# Revit family: SH-4502
name_source: partatom
category: Lighting Fixtures
revit_build: Autodesk Revit 2017 (Build: 20160225_1515(x64)
units: mm (PartAtom-declared; Revit-internal decimal feet)

## family parameters
Cut with Voids When Loaded = No
Host = Face
Light Source = Yes
Part Type = Normal
Room Calculation Point = No
Round Connector Dimension = Use Diameter
Shared = No

## types (2) — shared parameters
Body Material = Aluminum
Color Filter = 16777215
Default Elevation = 121.9 cm
Diffuser = Diffuser
Diffuser Material = Polycarbonate-anti uv
Dimming Lamp Color Temperature Shift = <None>
Emit Shape Visible in Rendering = No
Emit from Circle Diameter = 61.0 cm
Height = 33.6 cm
IP = IP44
Lamp = E27
Length = 22.7 cm
Manufacturer = SHOA
Model = SH-4502
Photometric Web File = 4376_V-TAC7WLEDBulbE27A60Thermoplastic3000K_1-5117.ies
Protection Class = Class I
Tilt Angle = 90.00°
URL = https://www.shoaco.com
Voltage/Frequency = 230v/50hz
Wattage. = 0 W
Width = 22.7 cm
Width base = 12.2 cm
color temperature = 3000K
consumption current = 0 A
website = www.shoaco.com

## per-type parameters (varying)
| type | Body Color |
| SH-4502(Black color-E27) | Black Body |
| SH-4502(White color-E27) | White Body |

## geometry (parser evidence)
native form markers: Sweep x5
no freeform markers — native parametric forms only
